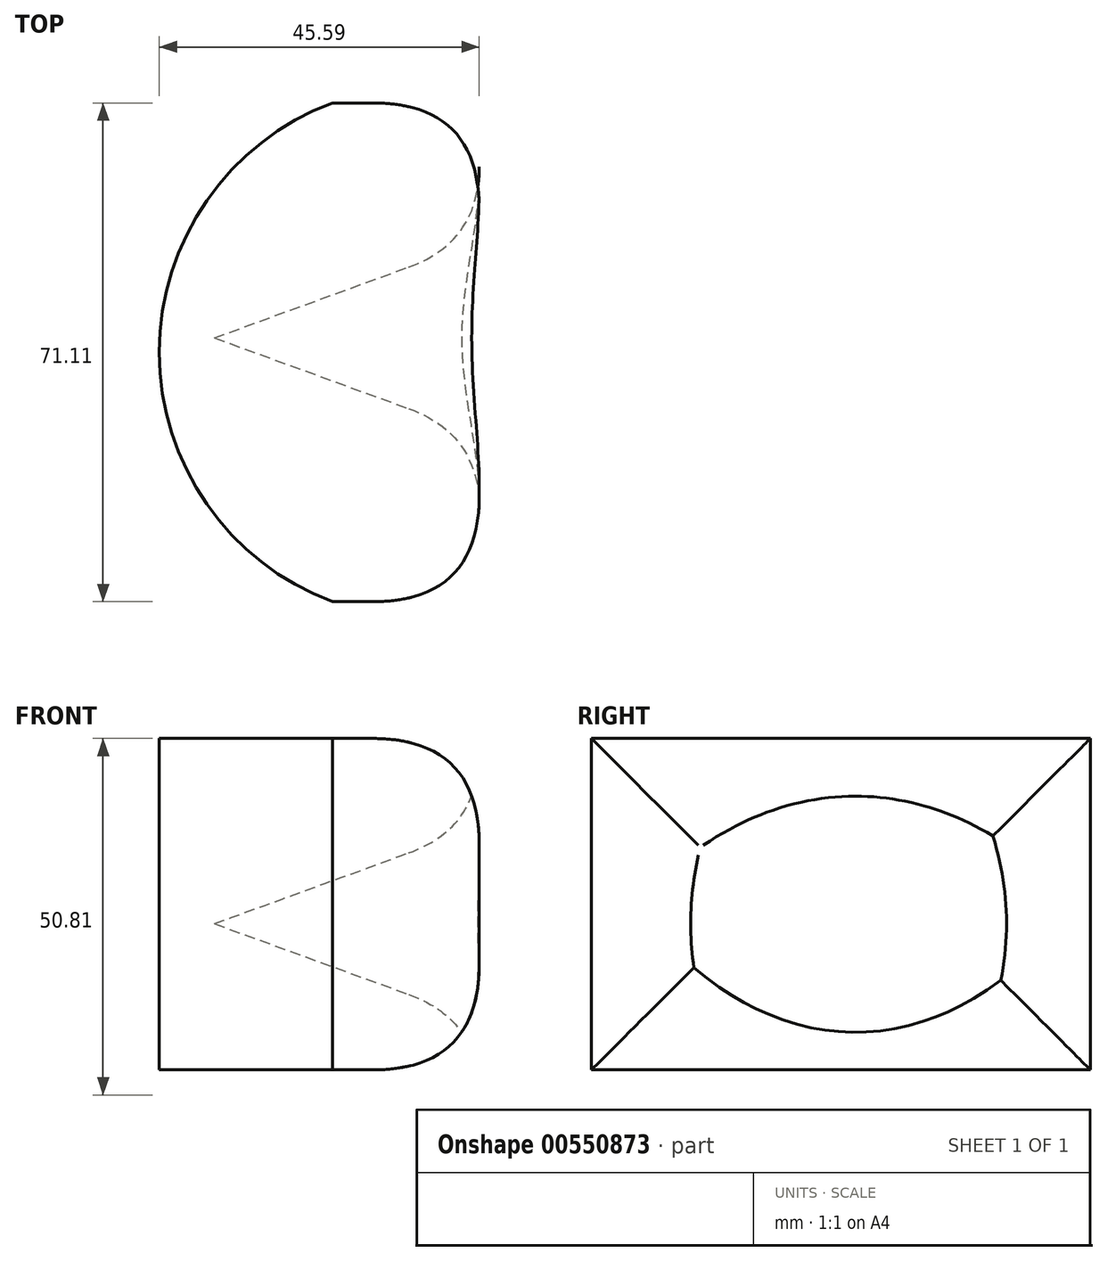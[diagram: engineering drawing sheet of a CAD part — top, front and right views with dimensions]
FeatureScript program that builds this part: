
annotation { "Feature Type Name" : "Feature", "Feature Type Description" : "" }
export const myFeature = defineFeature(function(context is Context, id is Id, definition is map)
    precondition{}
    {
        {
            var Q0;
            Q0=qCreatedBy(makeId("Top.planeOp"),FACE);
            var sketch = newSketch(context, id + "F0", { "sketchPlane" : qUnion([Q0])});
            skLineSegment(sketch, "E0", {"start": v(-59.2, 32) * mm, "end": v(-38.3, 32) * mm});
            skLineSegment(sketch, "E1", {"start": v(-38.3, 32) * mm, "end": v(-38.3, -39.1) * mm});
            skLineSegment(sketch, "E2", {"start": v(-38.3, -39.1) * mm, "end": v(-59.2, -39.1) * mm});
            skArc(sketch, "E3", {"start": v(-59.2, 32) * mm, "mid": v(-83.9, -3.55) * mm, "end": v(-59.2, -39.1) * mm});
            skSolve(sketch);
        }
        {
            var Q0;
            Q0=makeQuery(id+"F0.imprint","IMPRINT",FACE,{"disambiguationData":[TD([[makeQuery(id+"F0.imprint","IMPRINT",EDGE,{"derivedFrom":sQuery(id+"F0.wireOp",EDGE,"E0")}),-1.0]])]});
            extrude(context, id + "F1", {"entities" : qUnion([Q0]), "depth" : 47.24 * mm, "offsetDistance" : 25.4 * mm});
        }
        {
            var Q0;
            Q0=makeQuery(id+"F1.opExtrude","SWEPT_FACE",FACE,{"disambiguationData":[OSD([sQuery(id+"F0.wireOp",EDGE,"E1")])]});
            var sketch = newSketch(context, id + "F2", { "sketchPlane" : qUnion([Q0])});
            skCircle(sketch, "E4", {"center": v(-1.5, 20.84) * mm, "radius": 13.74 * mm});
            skSolve(sketch);
        }
        {
            var Q0;
            Q0=makeQuery(id+"F2.imprint","IMPRINT",FACE,{"disambiguationData":[TD([[makeQuery(id+"F2.imprint","IMPRINT",EDGE,{"derivedFrom":sQuery(id+"F2.wireOp",EDGE,"E4")}),1.0]])]});
            extrude(context, id + "F3", {"entities" : qUnion([Q0]), "operationType" : NewBodyOperationType.REMOVE, "oppositeDirection" : true, "depth" : 161.54 * mm, "offsetDistance" : 25.4 * mm, "hasDraft" : true, "draftAngle" : 20 * degree, "draftPullDirection" : true});
        }
        {
            var Q0;
            Q0=makeQuery(id+"F1.opExtrude","SWEPT_FACE",FACE,{"disambiguationData":[OSD([sQuery(id+"F0.wireOp",EDGE,"E1")])]});
            fillet(context, id + "F4", {"entities" : qUnion([Q0]), "radius" : 15.24 * mm, "tangentPropagation" : true, "rho" : 0.5, "crossSection" : FilletCrossSection.CONIC, "allowEdgeOverflow" : false});
        }
    });
